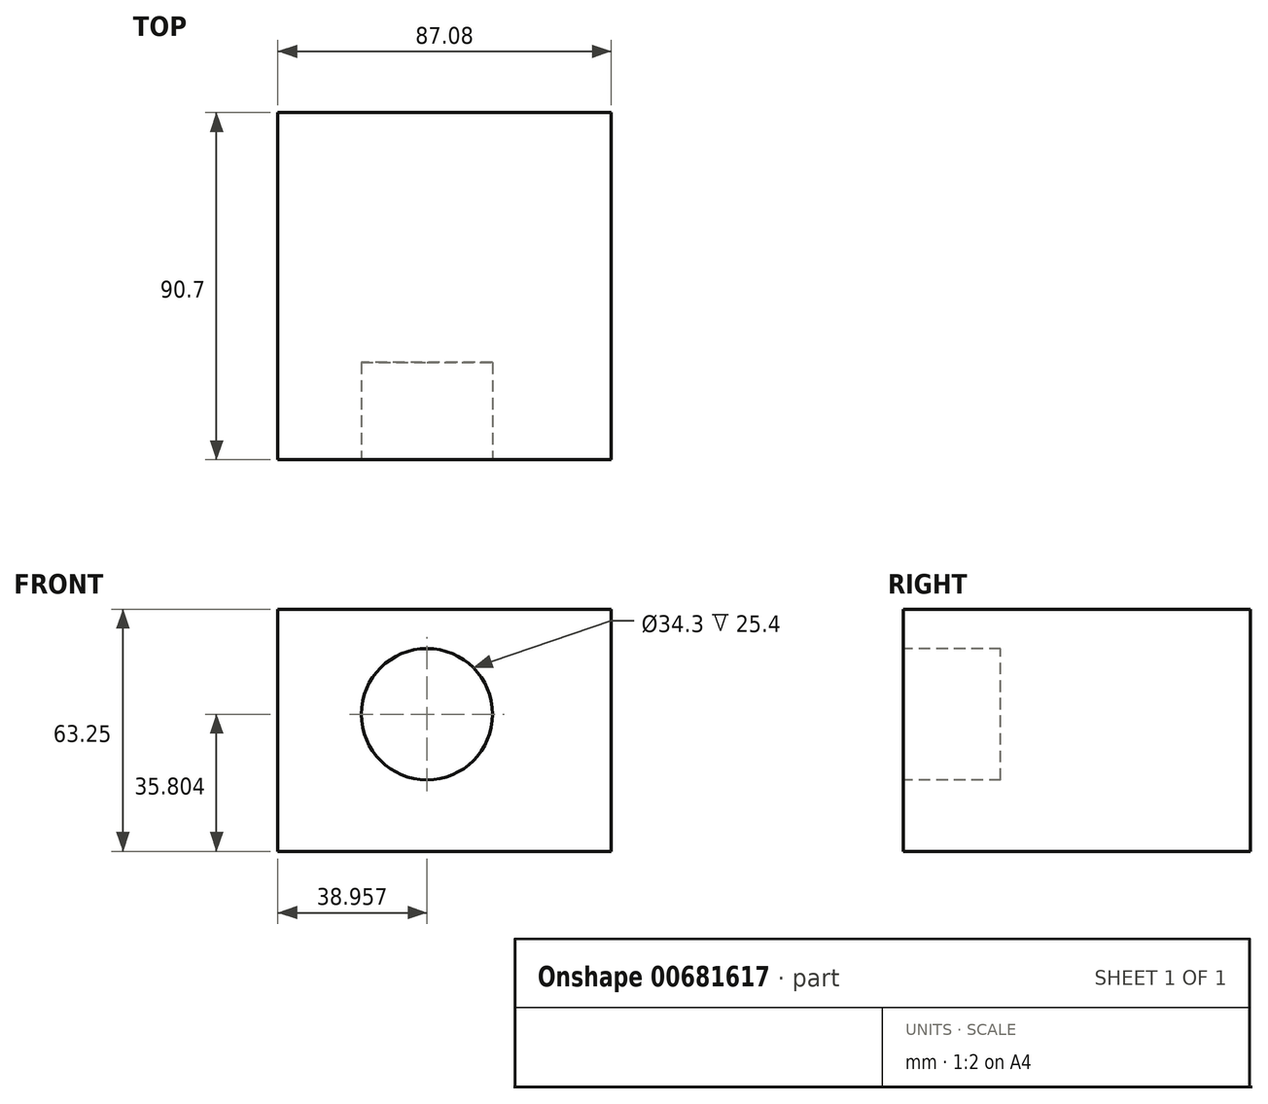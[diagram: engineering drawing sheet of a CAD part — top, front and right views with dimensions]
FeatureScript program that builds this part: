
annotation { "Feature Type Name" : "Feature", "Feature Type Description" : "" }
export const myFeature = defineFeature(function(context is Context, id is Id, definition is map)
    precondition{}
    {
        {
            var Q0;
            Q0=qCreatedBy(makeId("Top.planeOp"),FACE);
            var sketch = newSketch(context, id + "F0", { "sketchPlane" : qUnion([Q0])});
            skLineSegment(sketch, "E0.bottom", {"start": v(-36.57, 44.97) * mm, "end": v(50.5, 44.97) * mm});
            skLineSegment(sketch, "E0.top", {"start": v(-36.57, -45.73) * mm, "end": v(50.5, -45.73) * mm});
            skLineSegment(sketch, "E0.left", {"start": v(-36.57, 44.97) * mm, "end": v(-36.57, -45.73) * mm});
            skLineSegment(sketch, "E0.right", {"start": v(50.5, 44.97) * mm, "end": v(50.5, -45.73) * mm});
            skSolve(sketch);
        }
        {
            var Q0;
            Q0=makeQuery(id+"F0.imprint","IMPRINT",FACE,{"disambiguationData":[TD([[makeQuery(id+"F0.imprint","IMPRINT",EDGE,{"derivedFrom":sQuery(id+"F0.wireOp",EDGE,"E0.bottom")}),-1.0]])]});
            extrude(context, id + "F1", {"entities" : qUnion([Q0]), "depth" : 63.25 * mm, "offsetDistance" : 25.4 * mm});
        }
        {
            var Q0;
            Q0=qCreatedBy(makeId("Top.planeOp"),FACE);
            var sketch = newSketch(context, id + "F2", { "sketchPlane" : qUnion([Q0])});
            skCircle(sketch, "E1", {"center": v(0, 0) * mm, "radius": 10.98 * mm});
            skSolve(sketch);
        }
        {
            var Q0;
            Q0 = qSketchRegion(id + "F2", true);
            extrude(context, id + "F3", {"entities" : qUnion([Q0]), "operationType" : NewBodyOperationType.REMOVE, "oppositeDirection" : true, "depth" : 25.4 * mm, "offsetDistance" : 25.4 * mm});
        }
        {
            var Q0;
            Q0=makeQuery(id+"F1.opExtrude","SWEPT_FACE",FACE,{"disambiguationData":[OSD([sQuery(id+"F0.wireOp",EDGE,"E0.top")])]});
            var sketch = newSketch(context, id + "F4", { "sketchPlane" : qUnion([Q0])});
            skCircle(sketch, "E2", {"center": v(2.39, 35.8) * mm, "radius": 17.15 * mm});
            skSolve(sketch);
        }
        {
            var Q0;
            Q0=makeQuery(id+"F4.imprint","IMPRINT",FACE,{"disambiguationData":[TD([[makeQuery(id+"F4.imprint","IMPRINT",EDGE,{"derivedFrom":sQuery(id+"F4.wireOp",EDGE,"E2")}),1.0]])]});
            extrude(context, id + "F5", {"entities" : qUnion([Q0]), "operationType" : NewBodyOperationType.REMOVE, "oppositeDirection" : true, "depth" : 25.4 * mm, "offsetDistance" : 25.4 * mm});
        }
    });
